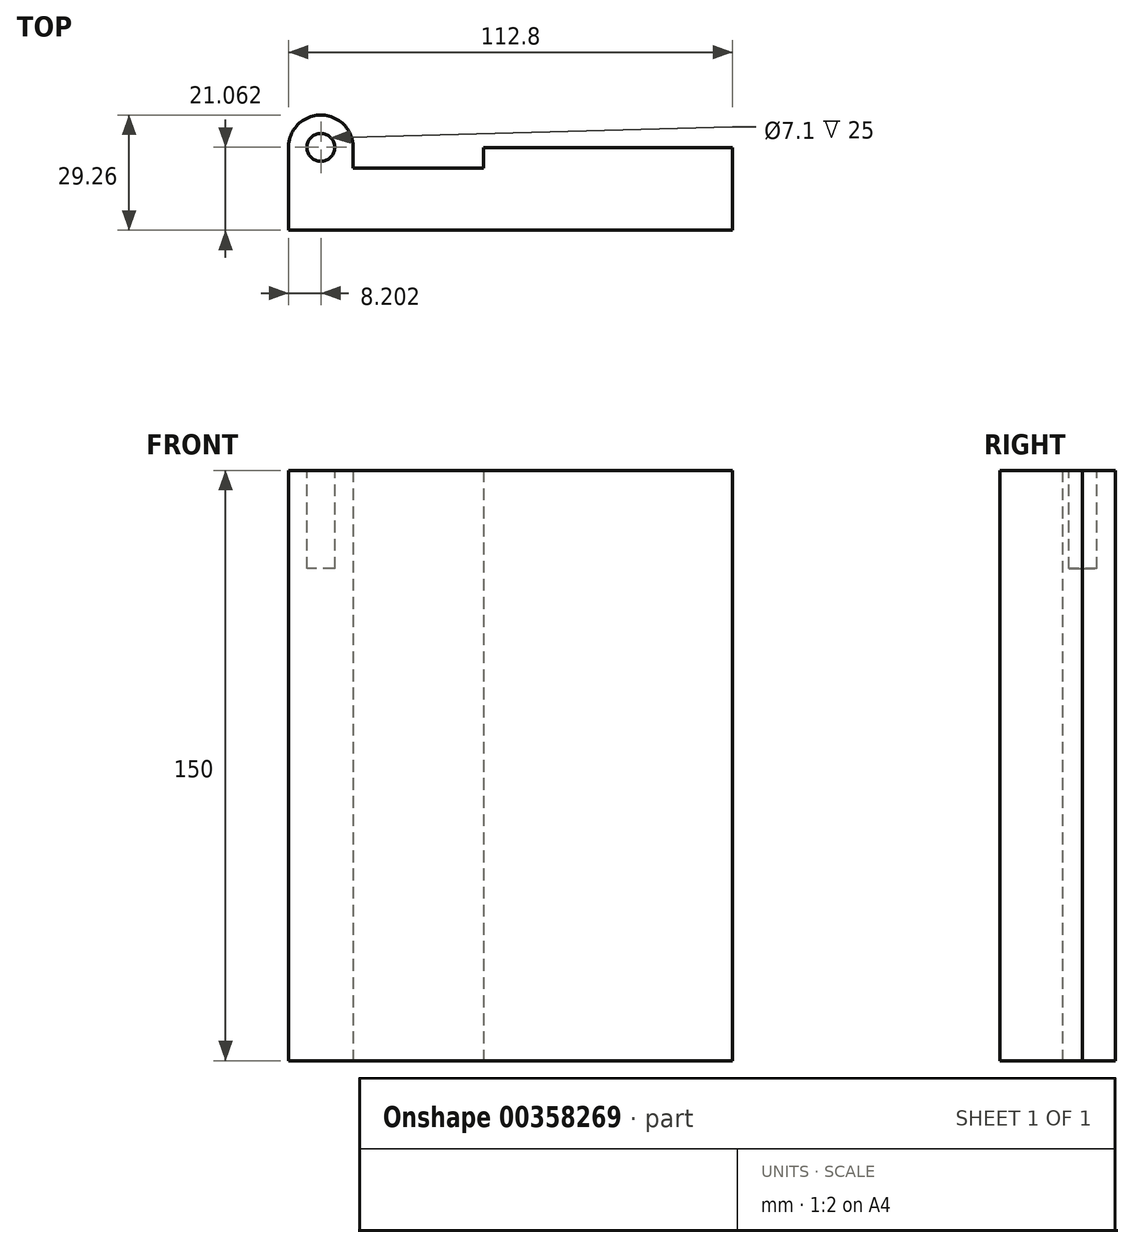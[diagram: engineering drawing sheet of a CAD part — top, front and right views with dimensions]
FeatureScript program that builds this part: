
annotation { "Feature Type Name" : "Feature", "Feature Type Description" : "" }
export const myFeature = defineFeature(function(context is Context, id is Id, definition is map)
    precondition{}
    {
        {
            var Q0;
            Q0=qCreatedBy(makeId("Top.planeOp"),FACE);
            var sketch = newSketch(context, id + "F0", { "sketchPlane" : qUnion([Q0])});
            skLineSegment(sketch, "E0", {"start": v(-57.1, 9.75) * mm, "end": v(-57.1, -11.45) * mm});
            skLineSegment(sketch, "E1", {"start": v(-57.1, -11.45) * mm, "end": v(55.7, -11.45) * mm});
            skLineSegment(sketch, "E2", {"start": v(55.7, -11.45) * mm, "end": v(55.7, 9.47) * mm});
            skLineSegment(sketch, "E3", {"start": v(55.7, 9.47) * mm, "end": v(-7.63, 9.47) * mm});
            skLineSegment(sketch, "E4", {"start": v(-7.63, 9.47) * mm, "end": v(-7.63, 4.38) * mm});
            skLineSegment(sketch, "E5", {"start": v(-7.63, 4.38) * mm, "end": v(-40.7, 4.38) * mm});
            skLineSegment(sketch, "E6", {"start": v(-40.7, 4.38) * mm, "end": v(-40.7, 9.47) * mm});
            skArc(sketch, "E7", {"start": v(-40.7, 9.47) * mm, "mid": v(-48.9, 17.81) * mm, "end": v(-57.1, 9.47) * mm});
            skSolve(sketch);
        }
        {
            var Q0;
            Q0 = qSketchRegion(id + "F0", true);
            extrude(context, id + "F1", {"entities" : qUnion([Q0]), "depth" : 150 * mm});
        }
        {
            var Q0;
            Q0=makeQuery(id+"F1.opExtrude","CAP_FACE",FACE,{"disambiguationData":[OSD([sQuery(id+"F0.wireOp",EDGE,"E0"),sQuery(id+"F0.wireOp",EDGE,"E1"),sQuery(id+"F0.wireOp",EDGE,"E2"),sQuery(id+"F0.wireOp",EDGE,"E3"),sQuery(id+"F0.wireOp",EDGE,"E4"),sQuery(id+"F0.wireOp",EDGE,"E5"),sQuery(id+"F0.wireOp",EDGE,"E6"),sQuery(id+"F0.wireOp",EDGE,"E7")])],"isStart":false});
            var sketch = newSketch(context, id + "F2", { "sketchPlane" : qUnion([Q0])});
            skCircle(sketch, "E8", {"center": v(-48.9, 9.61) * mm, "radius": 3.55 * mm});
            skSolve(sketch);
        }
        {
            var Q0;
            Q0=makeQuery(id+"F2.imprint","IMPRINT",FACE,{"disambiguationData":[TD([[makeQuery(id+"F2.imprint","IMPRINT",EDGE,{"derivedFrom":sQuery(id+"F2.wireOp",EDGE,"E8")}),1.0]])]});
            extrude(context, id + "F3", {"entities" : qUnion([Q0]), "operationType" : NewBodyOperationType.REMOVE, "oppositeDirection" : true, "depth" : 25 * mm});
        }
    });
